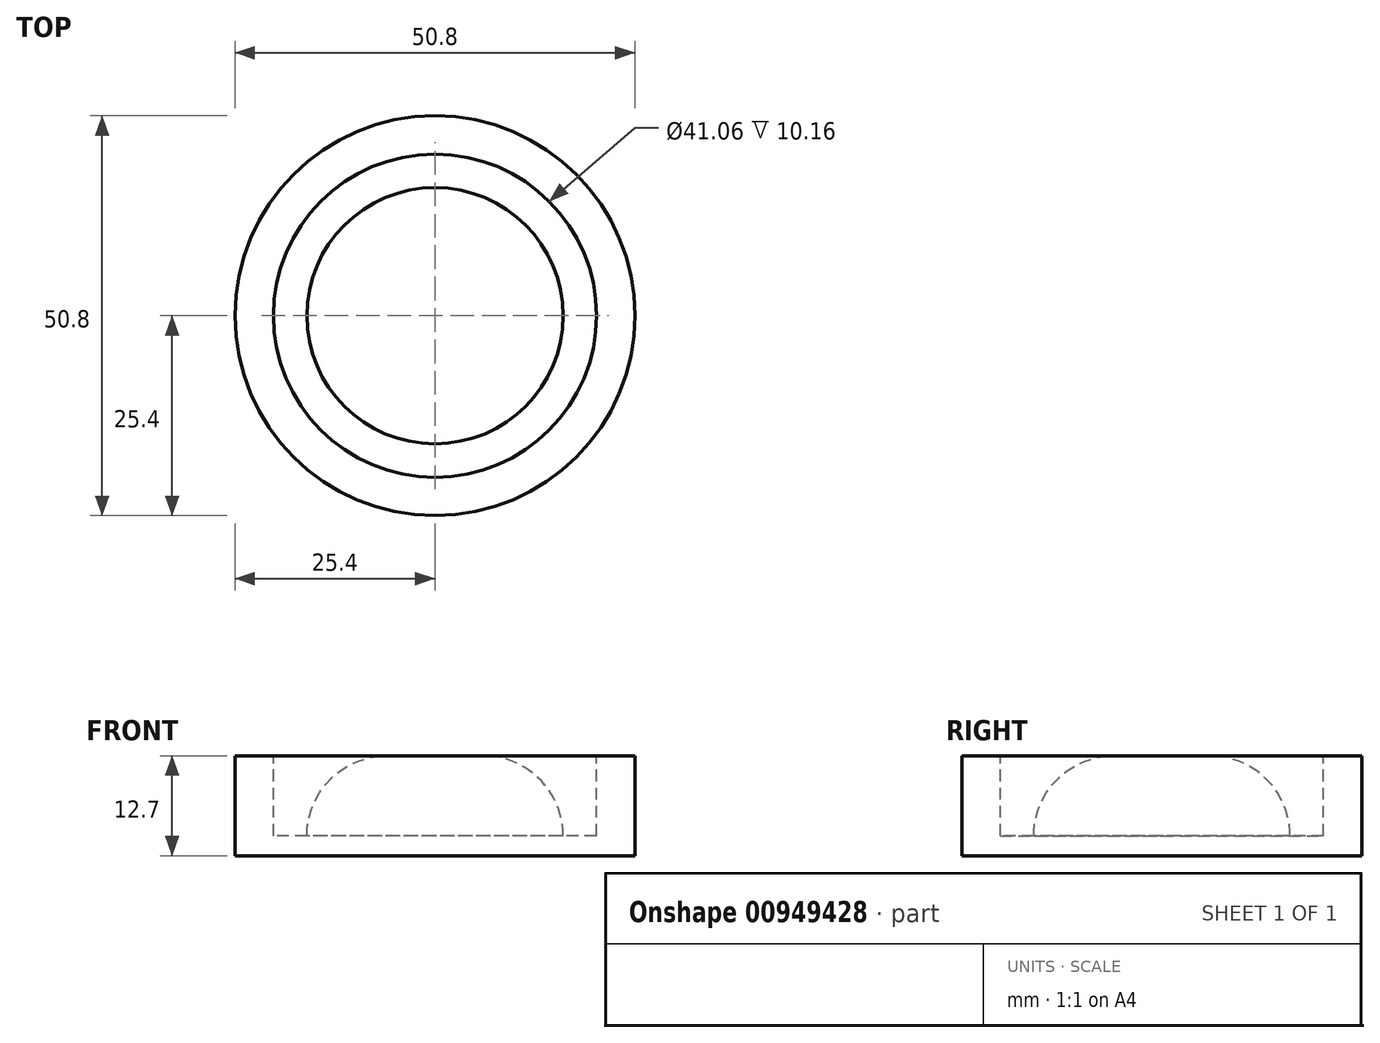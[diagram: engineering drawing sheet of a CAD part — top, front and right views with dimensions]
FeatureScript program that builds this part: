
annotation { "Feature Type Name" : "Feature", "Feature Type Description" : "" }
export const myFeature = defineFeature(function(context is Context, id is Id, definition is map)
    precondition{}
    {
        {
            var Q0;
            Q0=qCreatedBy(makeId("Top.planeOp"),FACE);
            var sketch = newSketch(context, id + "F0", { "sketchPlane" : qUnion([Q0])});
            skCircle(sketch, "E0", {"center": v(0, 0) * mm, "radius": 25.4 * mm});
            skSolve(sketch);
        }
        {
            var Q0;
            Q0 = qSketchRegion(id + "F0", true);
            var Q1;
            Q1=sQuery(id+"F0.wireOp",EDGE,"E0");
            extrude(context, id + "F1", {"entities" : qUnion([Q0]), "surfaceEntities" : qUnion([Q1]), "depth" : 12.7 * mm, "offsetDistance" : 25.4 * mm});
        }
        {
            var Q0;
            Q0=makeQuery(id+"F1.opExtrude","CAP_FACE",FACE,{"disambiguationData":[OSD([sQuery(id+"F0.wireOp",EDGE,"E0")])],"isStart":false});
            var sketch = newSketch(context, id + "F2", { "sketchPlane" : qUnion([Q0])});
            skCircle(sketch, "E1", {"center": v(0, 0) * mm, "radius": 20.53 * mm});
            skSolve(sketch);
        }
        {
            var Q0;
            Q0 = qSketchRegion(id + "F2", true);
            extrude(context, id + "F3", {"entities" : qUnion([Q0]), "operationType" : NewBodyOperationType.REMOVE, "oppositeDirection" : true, "depth" : 10.16 * mm, "offsetDistance" : 25.4 * mm});
        }
        {
            var Q0;
            Q0=makeQuery(id+"F3.boolean.opBoolean","COPY",FACE,{"derivedFrom":makeQuery(id+"F3.opExtrude","CAP_FACE",FACE,{"disambiguationData":[OSD([sQuery(id+"F2.wireOp",EDGE,"E1")])],"isStart":false})});
            var sketch = newSketch(context, id + "F4", { "sketchPlane" : qUnion([Q0])});
            skCircle(sketch, "E2", {"center": v(0, 0) * mm, "radius": 16.28 * mm});
            skSolve(sketch);
        }
        {
            var Q0;
            Q0=makeQuery(id+"F4.imprint","IMPRINT",FACE,{"disambiguationData":[TD([[makeQuery(id+"F4.imprint","IMPRINT",EDGE,{"derivedFrom":sQuery(id+"F4.wireOp",EDGE,"E2")}),1.0]])]});
            extrude(context, id + "F5", {"entities" : qUnion([Q0]), "operationType" : NewBodyOperationType.ADD, "depth" : 10.16 * mm, "offsetDistance" : 25.4 * mm});
        }
        {
            var Q0;
            Q0=makeQuery(id+"F5.opExtrude","CAP_EDGE",EDGE,{"disambiguationData":[OSD([sQuery(id+"F4.wireOp",EDGE,"E2")])],"isStart":false});
            fillet(context, id + "F6", {"entities" : qUnion([Q0]), "radius" : 10.16 * mm, "tangentPropagation" : true, "allowEdgeOverflow" : false});
        }
    });
